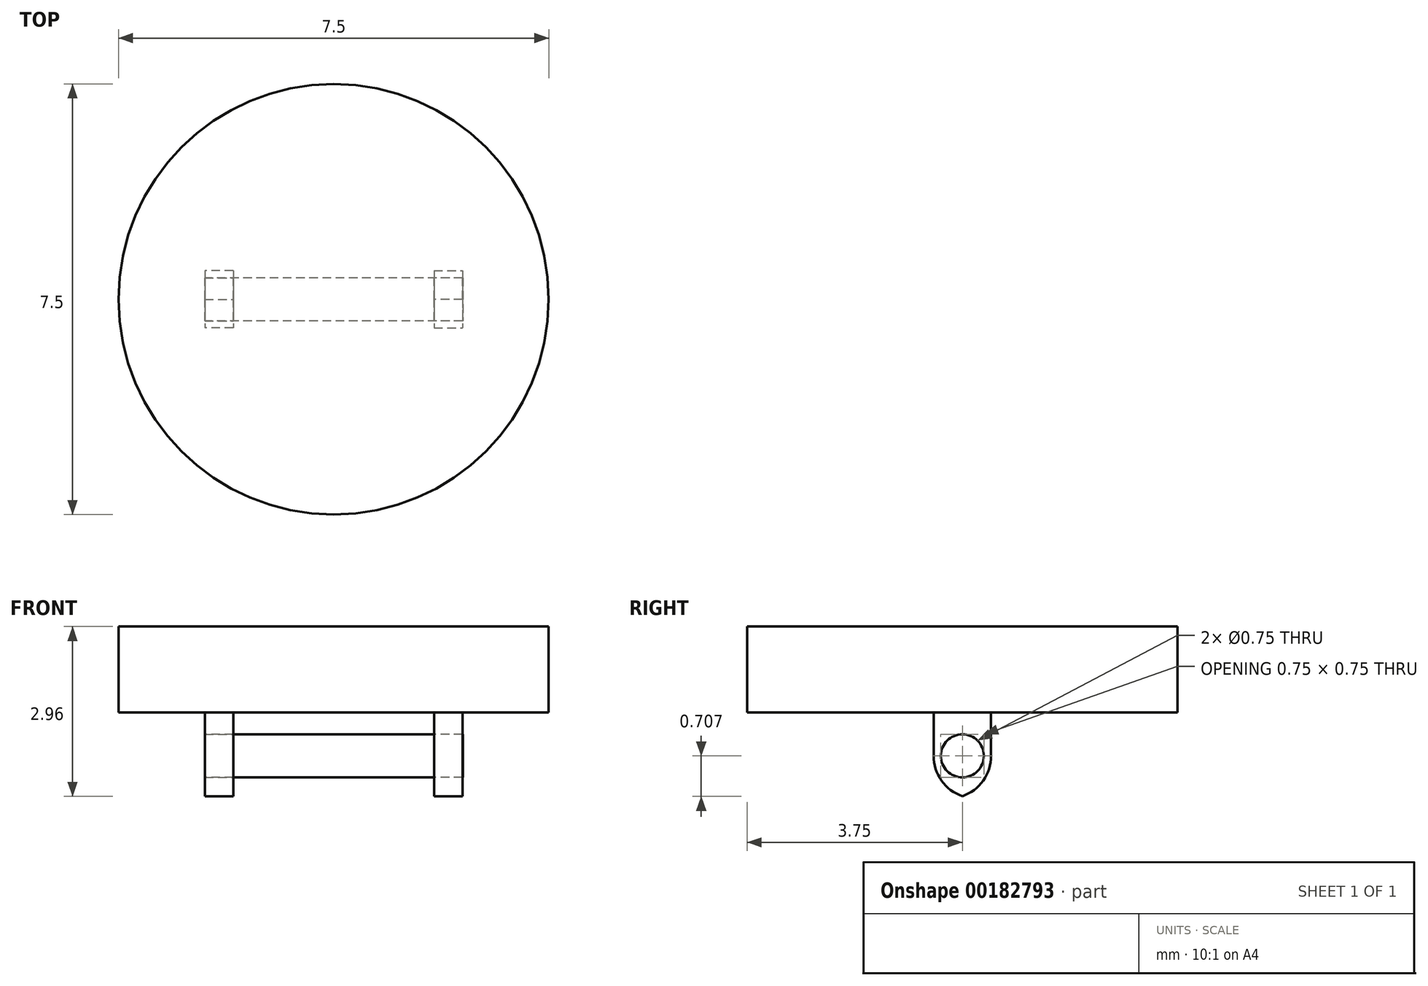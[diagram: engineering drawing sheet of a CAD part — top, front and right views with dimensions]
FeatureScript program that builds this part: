
annotation { "Feature Type Name" : "Feature", "Feature Type Description" : "" }
export const myFeature = defineFeature(function(context is Context, id is Id, definition is map)
    precondition{}
    {
        {
            var Q0;
            Q0=qCreatedBy(makeId("Top.planeOp"),FACE);
            var sketch = newSketch(context, id + "F0", { "sketchPlane" : qUnion([Q0])});
            skCircle(sketch, "E0", {"center": v(0, 0) * mm, "radius": 3.75 * mm});
            skSolve(sketch);
        }
        {
            var Q0;
            Q0 = qSketchRegion(id + "F0", true);
            extrude(context, id + "F1", {"entities" : qUnion([Q0]), "oppositeDirection" : true, "depth" : 1.5 * mm});
        }
        {
            var Q0;
            Q0=makeQuery(id+"F1.opExtrude","CAP_FACE",FACE,{"disambiguationData":[OSD([sQuery(id+"F0.wireOp",EDGE,"E0")])],"isStart":false});
            var sketch = newSketch(context, id + "F2", { "sketchPlane" : qUnion([Q0])});
            skLineSegment(sketch, "E1", {"start": v(0, 0) * mm, "end": v(2, 0) * mm});
            skLineSegment(sketch, "E2", {"start": v(2, 0) * mm, "end": v(-2, 0) * mm});
            skLineSegment(sketch, "E3.bottom", {"start": v(-1.75, -0.5) * mm, "end": v(-2.24, -0.5) * mm});
            skLineSegment(sketch, "E3.top", {"start": v(-1.75, 0.5) * mm, "end": v(-2.24, 0.5) * mm});
            skLineSegment(sketch, "E3.left", {"start": v(-1.75, -0.5) * mm, "end": v(-1.75, 0.5) * mm});
            skLineSegment(sketch, "E3.right", {"start": v(-2.24, -0.5) * mm, "end": v(-2.24, 0.5) * mm});
            skPoint(sketch, "E3.middle", {"position": v(-2, 0) * mm});
            skSolve(sketch);
        }
        {
            var Q0;
            {var subQ3=sQuery(id+"F2.wireOp",EDGE,"E3.bottom");Q0=makeQuery(id+"F2.imprint","IMPRINT",FACE,{"disambiguationData":[TD([[makeQuery(id+"F2.imprint","IMPRINT",EDGE,{"derivedFrom":subQ3}),-1.0]])]});}
            extrude(context, id + "F3", {"entities" : qUnion([Q0]), "operationType" : NewBodyOperationType.ADD, "depth" : 1.5 * mm});
        }
        {
            var Q0;
            Q0=makeQuery(id+"F3.opExtrude","SWEPT_FACE",FACE,{"disambiguationData":[OSD([sQuery(id+"F2.wireOp",EDGE,"E3.left")])]});
            var sketch = newSketch(context, id + "F4", { "sketchPlane" : qUnion([Q0])});
            skLineSegment(sketch, "E4", {"start": v(0, -3) * mm, "end": v(0, -2.25) * mm});
            skPoint(sketch, "E4.endSnap0", {"position": v(0, -1.5) * mm});
            skSolve(sketch);
        }
        {
            var Q0;
            Q0=sQuery(id+"F4.wireOp",VERTEX,"E4.end");
            var Q1;
            Q1=makeQuery(id+"F1.opExtrude","SWEPT_BODY",BODY,{"disambiguationData":[OSD([sQuery(id+"F0.wireOp",EDGE,"E0")])]});
            hole(context, id + "F5", {"style" : HoleStyle.SIMPLE, "endStyle" : HoleEndStyle.THROUGH, "holeDiameter" : 0.75 * mm, "locations" : qUnion([Q0]), "scope" : qUnion([Q1]), "isTappedThrough" : true});
        }
        {
            var Q0;
            Q0=makeQuery(id+"F3.opExtrude","CAP_EDGE",EDGE,{"disambiguationData":[OSD([sQuery(id+"F2.wireOp",EDGE,"E3.top")])],"isStart":false});
            var Q1;
            Q1=makeQuery(id+"F3.opExtrude","CAP_EDGE",EDGE,{"disambiguationData":[OSD([sQuery(id+"F2.wireOp",EDGE,"E3.bottom")])],"isStart":false});
            fillet(context, id + "F6", {"entities" : qUnion([Q0, Q1]), "radius" : 0.75 * mm, "tangentPropagation" : true, "allowEdgeOverflow" : false});
        }
        {
            var Q0;
            Q0=makeQuery(id+"F1.opExtrude","SWEPT_BODY",BODY,{"disambiguationData":[OSD([sQuery(id+"F0.wireOp",EDGE,"E0")])]});
            var Q1;
            Q1=qCreatedBy(makeId("Right.planeOp"),FACE);
            mirror(context, id + "F7", {"operationType" : NewBodyOperationType.ADD, "entities" : qUnion([Q0]), "mirrorPlane" : qUnion([Q1])});
        }
        {
            var Q0;
            Q0=makeQuery(id+"F3.opExtrude","SWEPT_FACE",FACE,{"disambiguationData":[OSD([sQuery(id+"F2.wireOp",EDGE,"E3.right")])]});
            var sketch = newSketch(context, id + "F8", { "sketchPlane" : qUnion([Q0])});
            skCircle(sketch, "E5", {"center": v(0, -2.25) * mm, "radius": 0.38 * mm});
            skSolve(sketch);
        }
        {
            var Q0;
            Q0=makeQuery(id+"F8.imprint","IMPRINT",FACE,{"disambiguationData":[TD([[makeQuery(id+"F8.imprint","IMPRINT",EDGE,{"derivedFrom":sQuery(id+"F8.wireOp",EDGE,"E5")}),-1.0]])]});
            extrude(context, id + "F9", {"entities" : qUnion([Q0]), "oppositeDirection" : true, "depth" : 4.5 * mm});
        }
    });
